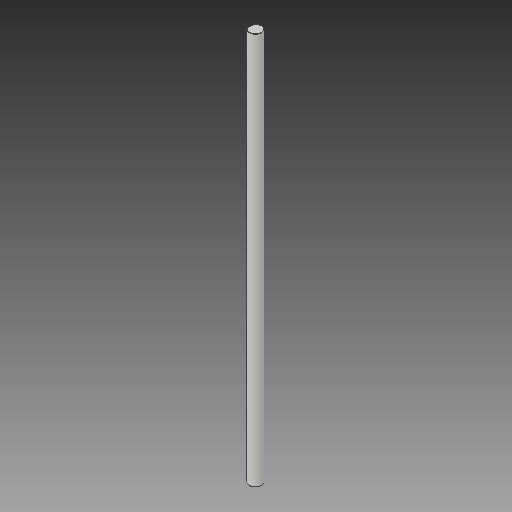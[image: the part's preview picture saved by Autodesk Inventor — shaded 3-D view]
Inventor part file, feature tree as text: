
AUTODESK INVENTOR PART (.ipt)
format: ipt  version: 2017 (Build 210142000, 142)  size: 82,432 bytes
history: native  units: in
note: dims shown in document units (in); Inventor stores cm internally (conversion verified against a paired STEP export)
features: chamfer x1
ambient origin geometry x8: Origin, YZ Plane, XZ Plane, XY Plane, X Axis, Y Axis, Z Axis, Center Point
bodies: Solid1 (feature_tree)
feature tree (1):
  chamfer  "Chamfer1"  [1 undecoded]
note: 1 required parameter value undecoded (feature->parameter linkage not recoverable at this tier; creation-order binding heuristic only, values carry confidence <= 0.55)
